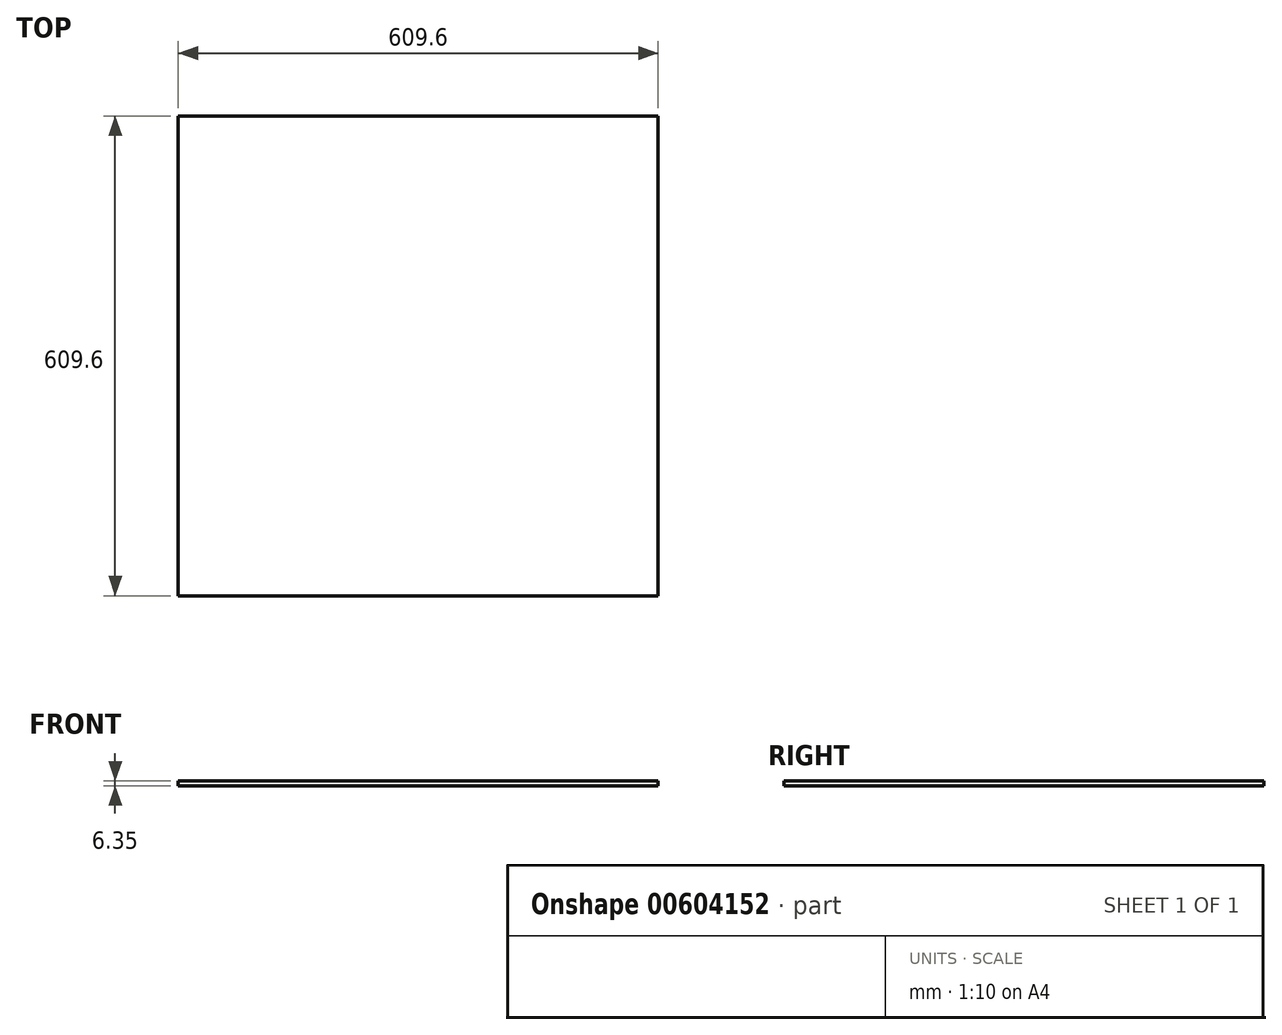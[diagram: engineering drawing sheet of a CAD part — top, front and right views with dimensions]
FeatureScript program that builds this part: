
annotation { "Feature Type Name" : "Feature", "Feature Type Description" : "" }
export const myFeature = defineFeature(function(context is Context, id is Id, definition is map)
    precondition{}
    {
        {
            var Q0;
            Q0=qCreatedBy(makeId("Top.planeOp"),FACE);
            var sketch = newSketch(context, id + "F0", { "sketchPlane" : qUnion([Q0])});
            skLineSegment(sketch, "E0.bottom", {"start": v(0, 0) * mm, "end": v(609.6, 0) * mm});
            skLineSegment(sketch, "E0.top", {"start": v(0, 609.6) * mm, "end": v(609.6, 609.6) * mm});
            skLineSegment(sketch, "E0.left", {"start": v(0, 0) * mm, "end": v(0, 609.6) * mm});
            skLineSegment(sketch, "E0.right", {"start": v(609.6, 0) * mm, "end": v(609.6, 609.6) * mm});
            skSolve(sketch);
        }
        {
            var Q0;
            Q0 = qSketchRegion(id + "F0", true);
            extrude(context, id + "F1", {"entities" : qUnion([Q0]), "depth" : 6.35 * mm, "offsetDistance" : 25 * mm});
        }
    });
